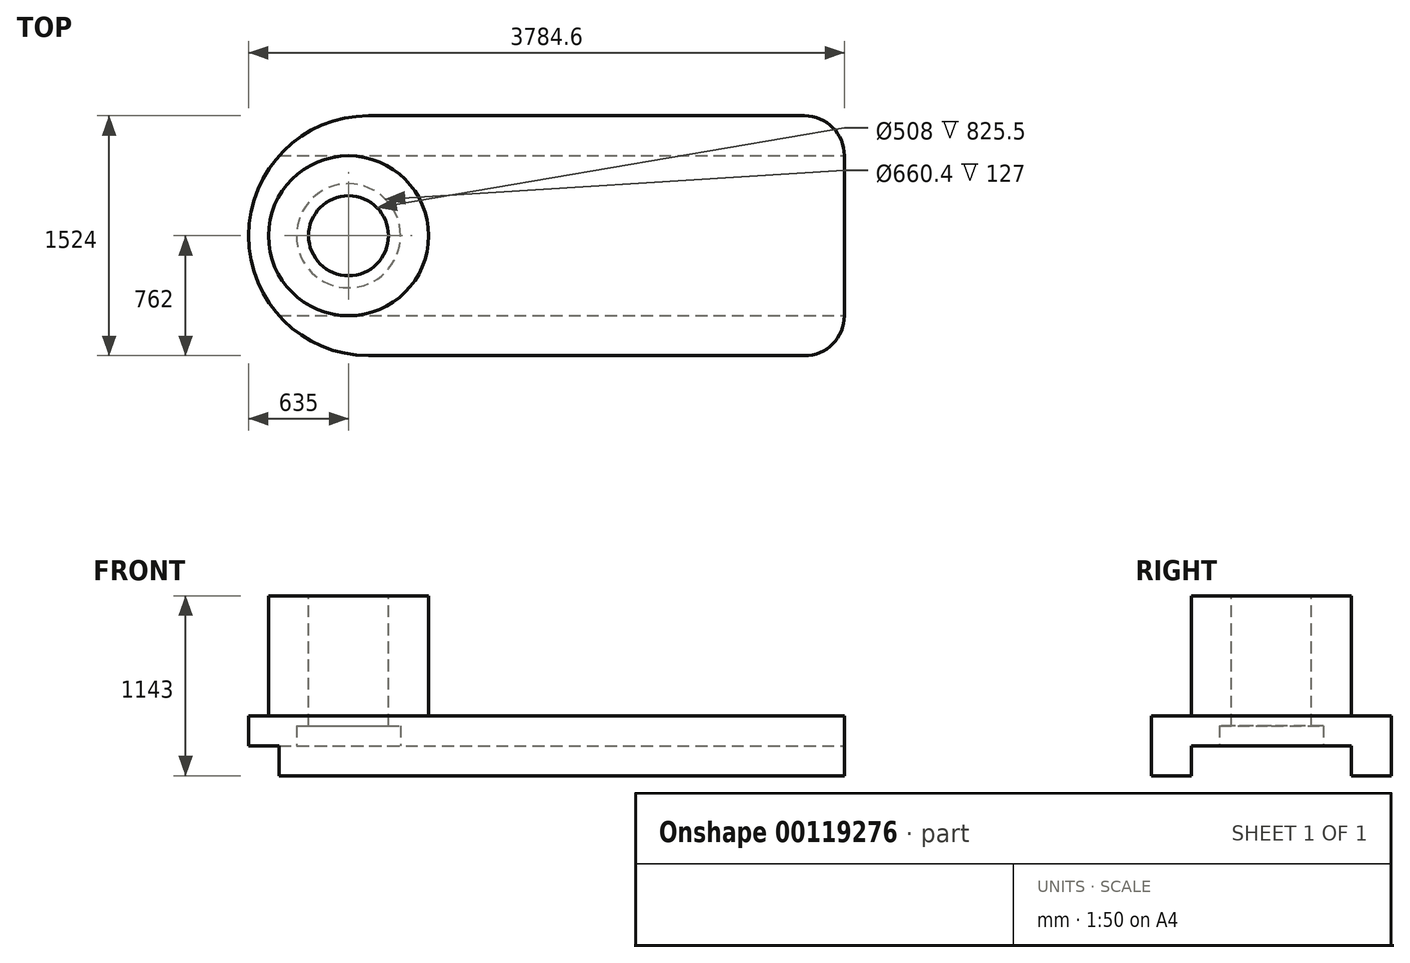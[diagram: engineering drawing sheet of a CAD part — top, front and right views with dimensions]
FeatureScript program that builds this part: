
annotation { "Feature Type Name" : "Feature", "Feature Type Description" : "" }
export const myFeature = defineFeature(function(context is Context, id is Id, definition is map)
    precondition{}
    {
        {
            var Q0;
            Q0=qCreatedBy(makeId("Top.planeOp"),FACE);
            var sketch = newSketch(context, id + "F0", { "sketchPlane" : qUnion([Q0])});
            skLineSegment(sketch, "E0.bottom", {"start": v(1384.3, -762) * mm, "end": v(-1384.3, -762) * mm});
            skLineSegment(sketch, "E0.top", {"start": v(1384.3, 762) * mm, "end": v(-1384.3, 762) * mm});
            skLineSegment(sketch, "E0.left", {"start": v(1384.3, -762) * mm, "end": v(1384.3, 762) * mm});
            skLineSegment(sketch, "E0.right", {"start": v(-1384.3, -762) * mm, "end": v(-1384.3, 762) * mm});
            skPoint(sketch, "E0.middle", {"position": v(0, 0) * mm});
            skCircle(sketch, "E1", {"center": v(-1384.3, 0) * mm, "radius": 762 * mm});
            skLineSegment(sketch, "E2.bottom", {"start": v(1384.3, 508) * mm, "end": v(1638.3, 508) * mm});
            skLineSegment(sketch, "E2.top", {"start": v(1390.65, -508) * mm, "end": v(1638.3, -508) * mm});
            skLineSegment(sketch, "E2.left", {"start": v(1384.3, 508) * mm, "end": v(1384.3, -501.65) * mm});
            skLineSegment(sketch, "E2.right", {"start": v(1638.3, 508) * mm, "end": v(1638.3, -508) * mm});
            skPoint(sketch, "E3.visualSharp", {"position": v(1384.3, -508) * mm});
            skArc(sketch, "E3.filletArc", {"start": v(1384.3, -501.65) * mm, "mid": v(1386.16, -506.14) * mm, "end": v(1390.65, -508) * mm});
            skArc(sketch, "E4", {"start": v(1384.3, -762) * mm, "mid": v(1563.9, -687.6) * mm, "end": v(1638.3, -508) * mm});
            skArc(sketch, "E5", {"start": v(1638.3, 508) * mm, "mid": v(1563.9, 687.6) * mm, "end": v(1384.3, 762) * mm});
            skSolve(sketch);
        }
        {
            var Q0;
            Q0 = qSketchRegion(id + "F0", true);
            extrude(context, id + "F1", {"entities" : qUnion([Q0]), "depth" : 381 * mm});
        }
        {
            var Q0;
            Q0=makeQuery(id+"F1.opExtrude","CAP_FACE",FACE,{"disambiguationData":[OSD([sQuery(id+"F0.wireOp",EDGE,"E0.bottom"),sQuery(id+"F0.wireOp",EDGE,"E0.top"),sQuery(id+"F0.wireOp",EDGE,"E0.right"),sQuery(id+"F0.wireOp",EDGE,"E1"),sQuery(id+"F0.wireOp",EDGE,"E2.right"),sQuery(id+"F0.wireOp",EDGE,"E4"),sQuery(id+"F0.wireOp",EDGE,"E5")])],"isStart":false});
            var sketch = newSketch(context, id + "F2", { "sketchPlane" : qUnion([Q0])});
            skSolve(sketch);
        }
        {
            var Q0;
            {var subQ3=sQuery(id+"F0.wireOp",EDGE,"E0.bottom");Q0=makeQuery(id+"F2.imprint","IMPRINT",FACE,{"disambiguationData":[TD([[makeQuery(id+"F2.imprint","IMPRINT",EDGE,{"derivedFrom":makeQuery(id+"F1.opExtrude","CAP_EDGE",EDGE,{"disambiguationData":[OSD([subQ3])],"isStart":false})}),-1.0]])]});}
            var sketch = newSketch(context, id + "F3", { "sketchPlane" : qUnion([Q0])});
            skCircle(sketch, "E6", {"center": v(-1511.3, 0) * mm, "radius": 508 * mm});
            skSolve(sketch);
        }
        {
            var Q0;
            Q0 = qSketchRegion(id + "F3", true);
            extrude(context, id + "F4", {"entities" : qUnion([Q0]), "operationType" : NewBodyOperationType.ADD, "depth" : 762 * mm});
        }
        {
            var Q0;
            Q0=makeQuery(id+"F4.opExtrude","CAP_FACE",FACE,{"disambiguationData":[OSD([sQuery(id+"F3.wireOp",EDGE,"E6")])],"isStart":false});
            var sketch = newSketch(context, id + "F5", { "sketchPlane" : qUnion([Q0])});
            skCircle(sketch, "E7", {"center": v(-1511.3, 0) * mm, "radius": 254 * mm});
            skSolve(sketch);
        }
        {
            var Q0;
            Q0 = qSketchRegion(id + "F5", true);
            extrude(context, id + "F6", {"entities" : qUnion([Q0]), "operationType" : NewBodyOperationType.REMOVE, "endBound" : BoundingType.THROUGH_ALL, "oppositeDirection" : true, "depth" : 25.4 * mm});
        }
        {
            var Q0;
            Q0=makeQuery(id+"F1.opExtrude","SWEPT_FACE",FACE,{"disambiguationData":[OSD([sQuery(id+"F0.wireOp",EDGE,"E2.right")])]});
            var sketch = newSketch(context, id + "F7", { "sketchPlane" : qUnion([Q0])});
            skLineSegment(sketch, "E8.bottom", {"start": v(-508, 0) * mm, "end": v(508, 0) * mm});
            skLineSegment(sketch, "E8.top", {"start": v(-508, 190.5) * mm, "end": v(508, 190.5) * mm});
            skLineSegment(sketch, "E8.left", {"start": v(-508, 0) * mm, "end": v(-508, 190.5) * mm});
            skLineSegment(sketch, "E8.right", {"start": v(508, 0) * mm, "end": v(508, 190.5) * mm});
            skSolve(sketch);
        }
        {
            var Q0;
            Q0 = qSketchRegion(id + "F7", true);
            extrude(context, id + "F8", {"entities" : qUnion([Q0]), "operationType" : NewBodyOperationType.REMOVE, "endBound" : BoundingType.THROUGH_ALL, "oppositeDirection" : true, "depth" : 25.4 * mm});
        }
        {
            var Q0;
            Q0=makeQuery(id+"F8.boolean.opBoolean","COPY",FACE,{"derivedFrom":makeQuery(id+"F8.opExtrude","SWEPT_FACE",FACE,{"disambiguationData":[OSD([sQuery(id+"F7.wireOp",EDGE,"E8.top")])]})});
            var sketch = newSketch(context, id + "F9", { "sketchPlane" : qUnion([Q0])});
            skCircle(sketch, "E9", {"center": v(-1511.3, 0) * mm, "radius": 330.2 * mm});
            skSolve(sketch);
        }
        {
            var Q0;
            Q0 = qSketchRegion(id + "F9", true);
            extrude(context, id + "F10", {"entities" : qUnion([Q0]), "operationType" : NewBodyOperationType.REMOVE, "oppositeDirection" : true, "depth" : 127 * mm});
        }
        {
            var Q0;
            Q0=makeQuery(id+"F1.opExtrude","SWEPT_FACE",FACE,{"disambiguationData":[OSD([sQuery(id+"F0.wireOp",EDGE,"E0.bottom")])]});
            cPlane(context, id + "F11", {"entities" : qUnion([Q0]), "cplaneType" : CPlaneType.OFFSET, "offset" : 254 * mm, "oppositeDirection" : true, "width" : 152.4 * mm, "height" : 152.4 * mm});
        }
    });
